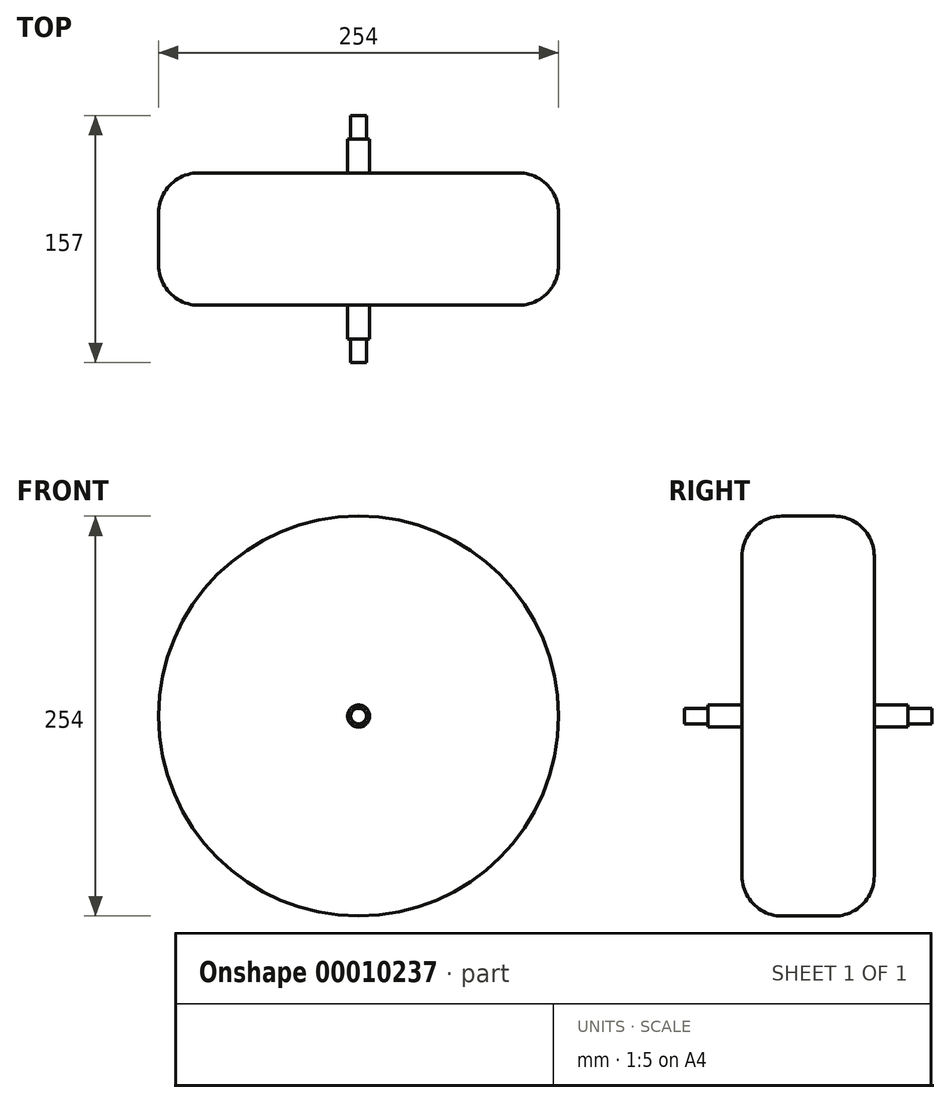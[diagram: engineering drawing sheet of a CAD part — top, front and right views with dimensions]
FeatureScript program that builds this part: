
annotation { "Feature Type Name" : "Feature", "Feature Type Description" : "" }
export const myFeature = defineFeature(function(context is Context, id is Id, definition is map)
    precondition{}
    {
        {
            var Q0;
            Q0=qCreatedBy(makeId("Front.planeOp"),FACE);
            var sketch = newSketch(context, id + "F0", { "sketchPlane" : qUnion([Q0])});
            skCircle(sketch, "E0", {"center": v(0, 0) * mm, "radius": 7 * mm});
            skSolve(sketch);
        }
        {
            var Q0;
            Q0=makeQuery(id+"F0.imprint","IMPRINT",FACE,{"disambiguationData":[TD([[makeQuery(id+"F0.imprint","IMPRINT",EDGE,{"derivedFrom":sQuery(id+"F0.wireOp",EDGE,"E0")}),1.0]])]});
            extrude(context, id + "F1", {"entities" : qUnion([Q0]), "depth" : 63.5 * mm});
        }
        {
            var Q0;
            Q0=makeQuery(id+"F1.opExtrude","CAP_FACE",FACE,{"disambiguationData":[OSD([sQuery(id+"F0.wireOp",EDGE,"E0")])],"isStart":false});
            var sketch = newSketch(context, id + "F2", { "sketchPlane" : qUnion([Q0])});
            skCircle(sketch, "E1", {"center": v(0, 0) * mm, "radius": 5 * mm});
            skSolve(sketch);
        }
        {
            var Q0;
            Q0=makeQuery(id+"F2.imprint","IMPRINT",FACE,{"disambiguationData":[TD([[makeQuery(id+"F2.imprint","IMPRINT",EDGE,{"derivedFrom":sQuery(id+"F2.wireOp",EDGE,"E1")}),1.0]])]});
            extrude(context, id + "F3", {"entities" : qUnion([Q0]), "operationType" : NewBodyOperationType.ADD, "depth" : 15 * mm});
        }
        {
            var Q0;
            Q0=qCreatedBy(makeId("Front.planeOp"),FACE);
            var sketch = newSketch(context, id + "F4", { "sketchPlane" : qUnion([Q0])});
            skCircle(sketch, "E2", {"center": v(0, 0) * mm, "radius": 127 * mm});
            skSolve(sketch);
        }
        {
            var Q0;
            Q0=makeQuery(id+"F4.imprint","IMPRINT",FACE,{"disambiguationData":[TD([[makeQuery(id+"F4.imprint","IMPRINT",EDGE,{"derivedFrom":sQuery(id+"F4.wireOp",EDGE,"E2")}),1.0]])]});
            extrude(context, id + "F5", {"entities" : qUnion([Q0]), "operationType" : NewBodyOperationType.ADD, "depth" : 42 * mm});
        }
        {
            var Q0;
            Q0=makeQuery(id+"F1.opExtrude","SWEPT_BODY",BODY,{"disambiguationData":[OSD([sQuery(id+"F0.wireOp",EDGE,"E0")])]});
            var Q1;
            Q1=makeQuery(id+"F5.boolean.opBoolean","MERGE",FACE,{"derivedFrom":[makeQuery(id+"F1.opExtrude","CAP_FACE",FACE,{"disambiguationData":[OSD([sQuery(id+"F0.wireOp",EDGE,"E0")])],"isStart":true}),makeQuery(id+"F5.opExtrude","CAP_FACE",FACE,{"disambiguationData":[OSD([sQuery(id+"F4.wireOp",EDGE,"E2")])],"isStart":true})]});
            mirror(context, id + "F6", {"operationType" : NewBodyOperationType.ADD, "entities" : qUnion([Q0]), "mirrorPlane" : qUnion([Q1])});
        }
        {
            var Q0;
            Q0=makeQuery(id+"F5.opExtrude","CAP_EDGE",EDGE,{"disambiguationData":[OSD([sQuery(id+"F4.wireOp",EDGE,"E2")])],"isStart":false});
            var Q1;
            Q1=makeQuery(id+"F6.opPattern","COPY",EDGE,{"derivedFrom":makeQuery(id+"F5.opExtrude","CAP_EDGE",EDGE,{"disambiguationData":[OSD([sQuery(id+"F4.wireOp",EDGE,"E2")])],"isStart":false}),"instanceName":"1"});
            fillet(context, id + "F7", {"entities" : qUnion([Q0, Q1]), "radius" : 25.4 * mm, "tangentPropagation" : true, "allowEdgeOverflow" : false});
        }
    });
